# Revit family: RN 84251 Optiflex-Flowpress-Raccordo
name_source: partatom
category: Rohrformteile
units: mm (PartAtom-declared; Revit-internal decimal feet)

## family parameters
Arbeitsebenenbasiert = Nein
Beim Laden mit Abzugskörper schneiden = Nein
Bemaßung runder Anschluss = Durchmesser verwenden
Gemeinsam genutzt = Nein
Immer vertikal = Ja
Teiletyp = Verbindung

## types (13) — shared parameters
1.010.00.2 Blattnummer der Richtlinie = 29
1.010.00.3 Ausgabedatum (Monat) der Richtlinie = 201308
1.010.00.4 Herstellername = R. Nussbaum AG
1.010.00.5 Revisionsdatum der Datei = 20190521
1.010.00.6 Webadresse des Herstellers = http://www.nussbaum.ch
1.100.00.4 Produktbezeichnung = Versorgung
1.110.00.2 Index = 5
1.110.00.4 Produktbezeichnung = Optiflex
1.960/3L.00.8 Link (URL) = https://www.nussbaum.ch
29.700.00.4 Produktname = Optiflex-F-Anschlussverschraubung, flachdichtend
29.700.00.5 Produktkennung = 2
29.700.00.6 Querschnittsform = 1
29.700.00.7 Nennweitensystem = DN
29.700.00.8 Nenndrucksystem = PN
29.710.02.4 Nenndruck = 10
29.710.02.5 max. zul. Überdruck [hPa] = 1000
29.710.02.7 max. zul. Dauer-Betriebsdruck [hPa] = 1000
29.710.02.9 max. zul. Dauer-Betriebstemperatur [°C] = 70
Connector Visibility = Nein
EnclosingSpace Visibility = Nein
Hersteller = R. Nussbaum AG
URL = https://www.nussbaum.ch

## per-type parameters (varying)
- DN=32x40: 1.800.00.3 TGA-Nummer=01900500000000000000000000000000000000000000000032000000000000000013; 1.800.00.4 Kommentarfeld=84251.37, Optiflex-F-Anschlussverschraubung, flachdichtend, DN=32x40, L=64; 1.810.00.3 Hersteller-Bestellnummer=84251.37; 1.810.00.4 DATANORM-Nummer=84251.37; 1.810.00.6 GTIN-Nummer=7612945813176; 29.710.02.10 Formstück-Gewicht [kg]=0.299; 29.710.02.3 Benennung=Optiflex-F-Anschlussverschraubung, flachdichtend, DN=32x40, L=64; CONNECTOR0_DIAMETER_dX_0r=40 mm; CONNECTOR0_dX_01=10 mm  [stored 0.0328084 ft]; CONNECTOR0_ref_dX=10 mm  [stored 0.0328084 ft]; CONNECTOR1_DIAMETER_dX_0r=40 mm; CONNECTOR1_dX_00=38 mm; CONNECTOR1_dX_01=64 mm; CONNECTOR1_ref_dX=38 mm; Modell=84251.37; R. Nussbaum AG 84251.21 de Visibility=Nein; R. Nussbaum AG 84251.22 de Visibility=Nein; R. Nussbaum AG 84251.23 de Visibility=Nein; R. Nussbaum AG 84251.24 de Visibility=Nein; R. Nussbaum AG 84251.25 de Visibility=Nein; R. Nussbaum AG 84251.26 de Visibility=Nein; R. Nussbaum AG 84251.27 de Visibility=Nein; R. Nussbaum AG 84251.28 de Visibility=Nein; R. Nussbaum AG 84251.29 de Visibility=Nein; R. Nussbaum AG 84251.30 de Visibility=Nein; R. Nussbaum AG 84251.35 de Visibility=Nein; R. Nussbaum AG 84251.36 de Visibility=Nein; R. Nussbaum AG 84251.37 de Visibility=Ja; Typenkommentare=Optiflex-Flowpress-Raccordo DN=32x40
- DN=25x40: 1.800.00.3 TGA-Nummer=01900500000000000000000000000000000000000000000032000000000000000012; 1.800.00.4 Kommentarfeld=84251.36, Optiflex-F-Anschlussverschraubung, flachdichtend, DN=25x40, L=54; 1.810.00.3 Hersteller-Bestellnummer=84251.36; 1.810.00.4 DATANORM-Nummer=84251.36; 1.810.00.6 GTIN-Nummer=7612945813169; 29.710.02.10 Formstück-Gewicht [kg]=0.224; 29.710.02.3 Benennung=Optiflex-F-Anschlussverschraubung, flachdichtend, DN=25x40, L=54; CONNECTOR0_DIAMETER_dX_0r=40 mm; CONNECTOR0_dX_01=10 mm  [stored 0.0328084 ft]; CONNECTOR0_ref_dX=10 mm  [stored 0.0328084 ft]; CONNECTOR1_DIAMETER_dX_0r=32 mm; CONNECTOR1_dX_00=34 mm; CONNECTOR1_dX_01=54 mm; CONNECTOR1_ref_dX=34 mm; Modell=84251.36; R. Nussbaum AG 84251.21 de Visibility=Nein; R. Nussbaum AG 84251.22 de Visibility=Nein; R. Nussbaum AG 84251.23 de Visibility=Nein; R. Nussbaum AG 84251.24 de Visibility=Nein; R. Nussbaum AG 84251.25 de Visibility=Nein; R. Nussbaum AG 84251.26 de Visibility=Nein; R. Nussbaum AG 84251.27 de Visibility=Nein; R. Nussbaum AG 84251.28 de Visibility=Nein; R. Nussbaum AG 84251.29 de Visibility=Nein; R. Nussbaum AG 84251.30 de Visibility=Nein; R. Nussbaum AG 84251.35 de Visibility=Nein; R. Nussbaum AG 84251.36 de Visibility=Ja; R. Nussbaum AG 84251.37 de Visibility=Nein; Typenkommentare=Optiflex-Flowpress-Raccordo DN=25x40
- DN=20x40: 1.800.00.3 TGA-Nummer=01900500000000000000000000000000000000000000000032000000000000000011; 1.800.00.4 Kommentarfeld=84251.35, Optiflex-F-Anschlussverschraubung, flachdichtend, DN=20x40, L=57; 1.810.00.3 Hersteller-Bestellnummer=84251.35; 1.810.00.4 DATANORM-Nummer=84251.35; 1.810.00.6 GTIN-Nummer=7612945813152; 29.710.02.10 Formstück-Gewicht [kg]=0.204; 29.710.02.3 Benennung=Optiflex-F-Anschlussverschraubung, flachdichtend, DN=20x40, L=57; CONNECTOR0_DIAMETER_dX_0r=40 mm; CONNECTOR0_dX_01=10 mm  [stored 0.0328084 ft]; CONNECTOR0_ref_dX=10 mm  [stored 0.0328084 ft]; CONNECTOR1_DIAMETER_dX_0r=25 mm  [stored 0.082021 ft]; CONNECTOR1_dX_00=36 mm; CONNECTOR1_dX_01=56 mm; CONNECTOR1_ref_dX=36 mm; Modell=84251.35; R. Nussbaum AG 84251.21 de Visibility=Nein; R. Nussbaum AG 84251.22 de Visibility=Nein; R. Nussbaum AG 84251.23 de Visibility=Nein; R. Nussbaum AG 84251.24 de Visibility=Nein; R. Nussbaum AG 84251.25 de Visibility=Nein; R. Nussbaum AG 84251.26 de Visibility=Nein; R. Nussbaum AG 84251.27 de Visibility=Nein; R. Nussbaum AG 84251.28 de Visibility=Nein; R. Nussbaum AG 84251.29 de Visibility=Nein; R. Nussbaum AG 84251.30 de Visibility=Nein; R. Nussbaum AG 84251.35 de Visibility=Ja; R. Nussbaum AG 84251.36 de Visibility=Nein; R. Nussbaum AG 84251.37 de Visibility=Nein; Typenkommentare=Optiflex-Flowpress-Raccordo DN=20x40
- DN=50: 1.800.00.3 TGA-Nummer=01900500000000000000000000000000000000000000000032000000000000000010; 1.800.00.4 Kommentarfeld=84251.30, Optiflex-F-Anschlussverschraubung, flachdichtend, DN=50, L=70; 1.810.00.3 Hersteller-Bestellnummer=84251.30; 1.810.00.4 DATANORM-Nummer=84251.30; 1.810.00.6 GTIN-Nummer=7612945745101; 29.710.02.10 Formstück-Gewicht [kg]=0.557; 29.710.02.3 Benennung=Optiflex-F-Anschlussverschraubung, flachdichtend, DN=50, L=70; CONNECTOR0_DIAMETER_dX_0r=50 mm; CONNECTOR0_dX_01=24 mm; CONNECTOR0_ref_dX=24 mm; CONNECTOR1_DIAMETER_dX_0r=50 mm; CONNECTOR1_dX_00=42 mm; CONNECTOR1_dX_01=70 mm; CONNECTOR1_ref_dX=42 mm; Modell=84251.30; R. Nussbaum AG 84251.21 de Visibility=Nein; R. Nussbaum AG 84251.22 de Visibility=Nein; R. Nussbaum AG 84251.23 de Visibility=Nein; R. Nussbaum AG 84251.24 de Visibility=Nein; R. Nussbaum AG 84251.25 de Visibility=Nein; R. Nussbaum AG 84251.26 de Visibility=Nein; R. Nussbaum AG 84251.27 de Visibility=Nein; R. Nussbaum AG 84251.28 de Visibility=Nein; R. Nussbaum AG 84251.29 de Visibility=Nein; R. Nussbaum AG 84251.30 de Visibility=Ja; R. Nussbaum AG 84251.35 de Visibility=Nein; R. Nussbaum AG 84251.36 de Visibility=Nein; R. Nussbaum AG 84251.37 de Visibility=Nein; Typenkommentare=Optiflex-Flowpress-Raccordo DN=50
- DN=40x50: 1.800.00.3 TGA-Nummer=01900500000000000000000000000000000000000000000032000000000000000009; 1.800.00.4 Kommentarfeld=84251.29, Optiflex-F-Anschlussverschraubung, flachdichtend, DN=40x50, L=69; 1.810.00.3 Hersteller-Bestellnummer=84251.29; 1.810.00.4 DATANORM-Nummer=84251.29; 1.810.00.6 GTIN-Nummer=7612945745095; 29.710.02.10 Formstück-Gewicht [kg]=0.514; 29.710.02.3 Benennung=Optiflex-F-Anschlussverschraubung, flachdichtend, DN=40x50, L=69; CONNECTOR0_DIAMETER_dX_0r=50 mm; CONNECTOR0_dX_01=24 mm; CONNECTOR0_ref_dX=24 mm; CONNECTOR1_DIAMETER_dX_0r=40 mm; CONNECTOR1_dX_00=43 mm; CONNECTOR1_dX_01=69 mm; CONNECTOR1_ref_dX=43 mm; Modell=84251.29; R. Nussbaum AG 84251.21 de Visibility=Nein; R. Nussbaum AG 84251.22 de Visibility=Nein; R. Nussbaum AG 84251.23 de Visibility=Nein; R. Nussbaum AG 84251.24 de Visibility=Nein; R. Nussbaum AG 84251.25 de Visibility=Nein; R. Nussbaum AG 84251.26 de Visibility=Nein; R. Nussbaum AG 84251.27 de Visibility=Nein; R. Nussbaum AG 84251.28 de Visibility=Nein; R. Nussbaum AG 84251.29 de Visibility=Ja; R. Nussbaum AG 84251.30 de Visibility=Nein; R. Nussbaum AG 84251.35 de Visibility=Nein; R. Nussbaum AG 84251.36 de Visibility=Nein; R. Nussbaum AG 84251.37 de Visibility=Nein; Typenkommentare=Optiflex-Flowpress-Raccordo DN=40x50
- DN=40: 1.800.00.3 TGA-Nummer=01900500000000000000000000000000000000000000000032000000000000000008; 1.800.00.4 Kommentarfeld=84251.28, Optiflex-F-Anschlussverschraubung, flachdichtend, DN=40, L=69; 1.810.00.3 Hersteller-Bestellnummer=84251.28; 1.810.00.4 DATANORM-Nummer=84251.28; 1.810.00.6 GTIN-Nummer=7612945745088; 29.710.02.10 Formstück-Gewicht [kg]=0.42; 29.710.02.3 Benennung=Optiflex-F-Anschlussverschraubung, flachdichtend, DN=40, L=69; CONNECTOR0_DIAMETER_dX_0r=40 mm; CONNECTOR0_dX_01=19 mm; CONNECTOR0_ref_dX=19 mm; CONNECTOR1_DIAMETER_dX_0r=40 mm; CONNECTOR1_dX_00=43 mm; CONNECTOR1_dX_01=69 mm; CONNECTOR1_ref_dX=43 mm; Modell=84251.28; R. Nussbaum AG 84251.21 de Visibility=Nein; R. Nussbaum AG 84251.22 de Visibility=Nein; R. Nussbaum AG 84251.23 de Visibility=Nein; R. Nussbaum AG 84251.24 de Visibility=Nein; R. Nussbaum AG 84251.25 de Visibility=Nein; R. Nussbaum AG 84251.26 de Visibility=Nein; R. Nussbaum AG 84251.27 de Visibility=Nein; R. Nussbaum AG 84251.28 de Visibility=Ja; R. Nussbaum AG 84251.29 de Visibility=Nein; R. Nussbaum AG 84251.30 de Visibility=Nein; R. Nussbaum AG 84251.35 de Visibility=Nein; R. Nussbaum AG 84251.36 de Visibility=Nein; R. Nussbaum AG 84251.37 de Visibility=Nein; Typenkommentare=Optiflex-Flowpress-Raccordo DN=40
- DN=32x25: 1.800.00.3 TGA-Nummer=01900500000000000000000000000000000000000000000032000000000000000007; 1.800.00.4 Kommentarfeld=84251.27, Optiflex-F-Anschlussverschraubung, flachdichtend, DN=32x25, L=69; 1.810.00.3 Hersteller-Bestellnummer=84251.27; 1.810.00.4 DATANORM-Nummer=84251.27; 1.810.00.6 GTIN-Nummer=7612945743480; 29.710.02.10 Formstück-Gewicht [kg]=0.26; 29.710.02.3 Benennung=Optiflex-F-Anschlussverschraubung, flachdichtend, DN=32x25, L=69; CONNECTOR0_DIAMETER_dX_0r=32 mm; CONNECTOR0_dX_01=19 mm; CONNECTOR0_ref_dX=19 mm; CONNECTOR1_DIAMETER_dX_0r=32 mm; CONNECTOR1_dX_00=43 mm; CONNECTOR1_dX_01=69 mm; CONNECTOR1_ref_dX=43 mm; Modell=84251.27; R. Nussbaum AG 84251.21 de Visibility=Nein; R. Nussbaum AG 84251.22 de Visibility=Nein; R. Nussbaum AG 84251.23 de Visibility=Nein; R. Nussbaum AG 84251.24 de Visibility=Nein; R. Nussbaum AG 84251.25 de Visibility=Nein; R. Nussbaum AG 84251.26 de Visibility=Nein; R. Nussbaum AG 84251.27 de Visibility=Ja; R. Nussbaum AG 84251.28 de Visibility=Nein; R. Nussbaum AG 84251.29 de Visibility=Nein; R. Nussbaum AG 84251.30 de Visibility=Nein; R. Nussbaum AG 84251.35 de Visibility=Nein; R. Nussbaum AG 84251.36 de Visibility=Nein; R. Nussbaum AG 84251.37 de Visibility=Nein; Typenkommentare=Optiflex-Flowpress-Raccordo DN=32x25
- DN=25: 1.800.00.3 TGA-Nummer=01900500000000000000000000000000000000000000000032000000000000000006; 1.800.00.4 Kommentarfeld=84251.26, Optiflex-F-Anschlussverschraubung, flachdichtend, DN=25, L=61; 1.810.00.3 Hersteller-Bestellnummer=84251.26; 1.810.00.4 DATANORM-Nummer=84251.26; 1.810.00.6 GTIN-Nummer=7612945743473; 29.710.02.10 Formstück-Gewicht [kg]=0.259; 29.710.02.3 Benennung=Optiflex-F-Anschlussverschraubung, flachdichtend, DN=25, L=61; CONNECTOR0_DIAMETER_dX_0r=32 mm; CONNECTOR0_dX_01=19 mm; CONNECTOR0_ref_dX=19 mm; CONNECTOR1_DIAMETER_dX_0r=25 mm  [stored 0.082021 ft]; CONNECTOR1_dX_00=34 mm; CONNECTOR1_dX_01=54 mm; CONNECTOR1_ref_dX=34 mm; Modell=84251.26; R. Nussbaum AG 84251.21 de Visibility=Nein; R. Nussbaum AG 84251.22 de Visibility=Nein; R. Nussbaum AG 84251.23 de Visibility=Nein; R. Nussbaum AG 84251.24 de Visibility=Nein; R. Nussbaum AG 84251.25 de Visibility=Nein; R. Nussbaum AG 84251.26 de Visibility=Ja; R. Nussbaum AG 84251.27 de Visibility=Nein; R. Nussbaum AG 84251.28 de Visibility=Nein; R. Nussbaum AG 84251.29 de Visibility=Nein; R. Nussbaum AG 84251.30 de Visibility=Nein; R. Nussbaum AG 84251.35 de Visibility=Nein; R. Nussbaum AG 84251.36 de Visibility=Nein; R. Nussbaum AG 84251.37 de Visibility=Nein; Typenkommentare=Optiflex-Flowpress-Raccordo DN=25
- DN=20x25: 1.800.00.3 TGA-Nummer=01900500000000000000000000000000000000000000000032000000000000000005; 1.800.00.4 Kommentarfeld=84251.25, Optiflex-F-Anschlussverschraubung, flachdichtend, DN=20x25, L=57; 1.810.00.3 Hersteller-Bestellnummer=84251.25; 1.810.00.4 DATANORM-Nummer=84251.25; 1.810.00.6 GTIN-Nummer=7612945743466; 29.710.02.10 Formstück-Gewicht [kg]=0.22; 29.710.02.3 Benennung=Optiflex-F-Anschlussverschraubung, flachdichtend, DN=20x25, L=57; CONNECTOR0_DIAMETER_dX_0r=32 mm; CONNECTOR0_dX_01=19 mm; CONNECTOR0_ref_dX=19 mm; CONNECTOR1_DIAMETER_dX_0r=20 mm; CONNECTOR1_dX_00=37 mm; CONNECTOR1_dX_01=57 mm; CONNECTOR1_ref_dX=37 mm; Modell=84251.25; R. Nussbaum AG 84251.21 de Visibility=Nein; R. Nussbaum AG 84251.22 de Visibility=Nein; R. Nussbaum AG 84251.23 de Visibility=Nein; R. Nussbaum AG 84251.24 de Visibility=Nein; R. Nussbaum AG 84251.25 de Visibility=Ja; R. Nussbaum AG 84251.26 de Visibility=Nein; R. Nussbaum AG 84251.27 de Visibility=Nein; R. Nussbaum AG 84251.28 de Visibility=Nein; R. Nussbaum AG 84251.29 de Visibility=Nein; R. Nussbaum AG 84251.30 de Visibility=Nein; R. Nussbaum AG 84251.35 de Visibility=Nein; R. Nussbaum AG 84251.36 de Visibility=Nein; R. Nussbaum AG 84251.37 de Visibility=Nein; Typenkommentare=Optiflex-Flowpress-Raccordo DN=20x25
- DN=15: 1.800.00.3 TGA-Nummer=01900500000000000000000000000000000000000000000032000000000000000004; 1.800.00.4 Kommentarfeld=84251.24, Optiflex-F-Anschlussverschraubung, flachdichtend, DN=15, L=46; 1.810.00.3 Hersteller-Bestellnummer=84251.24; 1.810.00.4 DATANORM-Nummer=84251.24; 1.810.00.6 GTIN-Nummer=7612945743459; 29.710.02.10 Formstück-Gewicht [kg]=0.081; 29.710.02.3 Benennung=Optiflex-F-Anschlussverschraubung, flachdichtend, DN=15, L=46; CONNECTOR0_DIAMETER_dX_0r=20 mm; CONNECTOR0_dX_01=15 mm  [stored 0.0492126 ft]; CONNECTOR0_ref_dX=15 mm  [stored 0.0492126 ft]; CONNECTOR1_DIAMETER_dX_0r=15 mm  [stored 0.0492126 ft]; CONNECTOR1_dX_00=32 mm; CONNECTOR1_dX_01=46 mm; CONNECTOR1_ref_dX=32 mm; Modell=84251.24; R. Nussbaum AG 84251.21 de Visibility=Nein; R. Nussbaum AG 84251.22 de Visibility=Nein; R. Nussbaum AG 84251.23 de Visibility=Nein; R. Nussbaum AG 84251.24 de Visibility=Ja; R. Nussbaum AG 84251.25 de Visibility=Nein; R. Nussbaum AG 84251.26 de Visibility=Nein; R. Nussbaum AG 84251.27 de Visibility=Nein; R. Nussbaum AG 84251.28 de Visibility=Nein; R. Nussbaum AG 84251.29 de Visibility=Nein; R. Nussbaum AG 84251.30 de Visibility=Nein; R. Nussbaum AG 84251.35 de Visibility=Nein; R. Nussbaum AG 84251.36 de Visibility=Nein; R. Nussbaum AG 84251.37 de Visibility=Nein; Typenkommentare=Optiflex-Flowpress-Raccordo DN=15
- DN=15x1: 1.800.00.3 TGA-Nummer=01900500000000000000000000000000000000000000000032000000000000000003; 1.800.00.4 Kommentarfeld=84251.23, Optiflex-F-Anschlussverschraubung, flachdichtend, DN=15x10, L=47; 1.810.00.3 Hersteller-Bestellnummer=84251.23; 1.810.00.4 DATANORM-Nummer=84251.23; 1.810.00.6 GTIN-Nummer=7612945743442; 29.710.02.10 Formstück-Gewicht [kg]=0.065; 29.710.02.3 Benennung=Optiflex-F-Anschlussverschraubung, flachdichtend, DN=15x10, L=47; CONNECTOR0_DIAMETER_dX_0r=15 mm  [stored 0.0492126 ft]; CONNECTOR0_dX_01=13 mm; CONNECTOR0_ref_dX=13 mm; CONNECTOR1_DIAMETER_dX_0r=15 mm  [stored 0.0492126 ft]; CONNECTOR1_dX_00=33 mm; CONNECTOR1_dX_01=47 mm; CONNECTOR1_ref_dX=33 mm; Modell=84251.23; R. Nussbaum AG 84251.21 de Visibility=Nein; R. Nussbaum AG 84251.22 de Visibility=Nein; R. Nussbaum AG 84251.23 de Visibility=Ja; R. Nussbaum AG 84251.24 de Visibility=Nein; R. Nussbaum AG 84251.25 de Visibility=Nein; R. Nussbaum AG 84251.26 de Visibility=Nein; R. Nussbaum AG 84251.27 de Visibility=Nein; R. Nussbaum AG 84251.28 de Visibility=Nein; R. Nussbaum AG 84251.29 de Visibility=Nein; R. Nussbaum AG 84251.30 de Visibility=Nein; R. Nussbaum AG 84251.35 de Visibility=Nein; R. Nussbaum AG 84251.36 de Visibility=Nein; R. Nussbaum AG 84251.37 de Visibility=Nein; Typenkommentare=Optiflex-Flowpress-Raccordo DN=15x10
- DN=12x20: 1.800.00.3 TGA-Nummer=01900500000000000000000000000000000000000000000032000000000000000002; 1.800.00.4 Kommentarfeld=84251.22, Optiflex-F-Anschlussverschraubung, flachdichtend, DN=12x20, L=45; 1.810.00.3 Hersteller-Bestellnummer=84251.22; 1.810.00.4 DATANORM-Nummer=84251.22; 1.810.00.6 GTIN-Nummer=7612945743435; 29.710.02.10 Formstück-Gewicht [kg]=0.073; 29.710.02.3 Benennung=Optiflex-F-Anschlussverschraubung, flachdichtend, DN=12x20, L=45; CONNECTOR0_DIAMETER_dX_0r=20 mm; CONNECTOR0_dX_01=15 mm  [stored 0.0492126 ft]; CONNECTOR0_ref_dX=15 mm  [stored 0.0492126 ft]; CONNECTOR1_DIAMETER_dX_0r=12 mm  [stored 0.0393701 ft]; CONNECTOR1_dX_00=31 mm; CONNECTOR1_dX_01=45 mm; CONNECTOR1_ref_dX=31 mm; Modell=84251.22; R. Nussbaum AG 84251.21 de Visibility=Nein; R. Nussbaum AG 84251.22 de Visibility=Ja; R. Nussbaum AG 84251.23 de Visibility=Nein; R. Nussbaum AG 84251.24 de Visibility=Nein; R. Nussbaum AG 84251.25 de Visibility=Nein; R. Nussbaum AG 84251.26 de Visibility=Nein; R. Nussbaum AG 84251.27 de Visibility=Nein; R. Nussbaum AG 84251.28 de Visibility=Nein; R. Nussbaum AG 84251.29 de Visibility=Nein; R. Nussbaum AG 84251.30 de Visibility=Nein; R. Nussbaum AG 84251.35 de Visibility=Nein; R. Nussbaum AG 84251.36 de Visibility=Nein; R. Nussbaum AG 84251.37 de Visibility=Nein; Typenkommentare=Optiflex-Flowpress-Raccordo DN=12x20
- DN=15x10: 1.800.00.3 TGA-Nummer=01900500000000000000000000000000000000000000000032000000000000000001; 1.800.00.4 Kommentarfeld=84251.21, Optiflex-F-Anschlussverschraubung, flachdichtend, DN=15x10, L=39; 1.810.00.3 Hersteller-Bestellnummer=84251.21; 1.810.00.4 DATANORM-Nummer=84251.21; 1.810.00.6 GTIN-Nummer=7612945743428; 29.710.02.10 Formstück-Gewicht [kg]=0.046; 29.710.02.3 Benennung=Optiflex-F-Anschlussverschraubung, flachdichtend, DN=15x10, L=39; CONNECTOR0_DIAMETER_dX_0r=15 mm  [stored 0.0492126 ft]; CONNECTOR0_dX_01=13 mm; CONNECTOR0_ref_dX=13 mm; CONNECTOR1_DIAMETER_dX_0r=12 mm  [stored 0.0393701 ft]; CONNECTOR1_dX_00=25 mm  [stored 0.082021 ft]; CONNECTOR1_dX_01=39 mm; CONNECTOR1_ref_dX=25 mm  [stored 0.082021 ft]; Modell=84251.21; R. Nussbaum AG 84251.21 de Visibility=Ja; R. Nussbaum AG 84251.22 de Visibility=Nein; R. Nussbaum AG 84251.23 de Visibility=Nein; R. Nussbaum AG 84251.24 de Visibility=Nein; R. Nussbaum AG 84251.25 de Visibility=Nein; R. Nussbaum AG 84251.26 de Visibility=Nein; R. Nussbaum AG 84251.27 de Visibility=Nein; R. Nussbaum AG 84251.28 de Visibility=Nein; R. Nussbaum AG 84251.29 de Visibility=Nein; R. Nussbaum AG 84251.30 de Visibility=Nein; R. Nussbaum AG 84251.35 de Visibility=Nein; R. Nussbaum AG 84251.36 de Visibility=Nein; R. Nussbaum AG 84251.37 de Visibility=Nein; Typenkommentare=Optiflex-Flowpress-Raccordo DN=15x10

note: [stored X ft] marks values corroborated as IEEE doubles in the binary element streams (Revit-internal decimal feet)

## geometry (parser evidence)
native form markers: Sweep x2
no freeform markers — native parametric forms only
